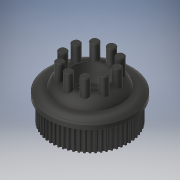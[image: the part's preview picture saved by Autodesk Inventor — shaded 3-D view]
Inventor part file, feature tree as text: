
AUTODESK INVENTOR PART (.ipt)
format: ipt  version: 2019.2 (Build 232265000, 265)  size: 961,536 bytes
history: native  units: mm
features: sketch x6, extrude x5, chamfer x4, fillet x3, other x1, pattern_circular x1, plane x1
ambient origin geometry x8: Origin, YZ Plane, XZ Plane, XY Plane, X Axis, Y Axis, Z Axis, Center Point
bodies: Solid1 (feature_tree)
feature tree (21):
  other  "gates_P60-3M-09AL.ipt"
  extrude  "Extrusion1"  Depth=7.0mm
  fillet  "Fillet1"  Radius=7.0mm
  extrude  "Extrusion2"  Depth=10.0mm
  chamfer  "Chamfer1"  Distance=18.0mm
  pattern_circular  "Circular Pattern1"  Count=10 Angle=360.0deg
  plane  "Work Plane1"
  sketch  "Sketch3"  dims[d9=0.5mm d10=2.0mm d11=45.0deg d12=100.0mm d13=360.0deg]
  extrude  "Extrusion3"  Depth=0.938mm
  chamfer  "Chamfer2"  Distance=2.4mm
  extrude  "Extrusion8"  Depth=7.0mm TaperAngle=0.0deg
  extrude  "Extrusion9"  Depth=7.0mm TaperAngle=45.0deg
  chamfer  "Chamfer5"  Distance=1.2mm
  fillet  "Fillet4"  Radius=10.0mm
  chamfer  "Chamfer6"  Distance=56.54mm
  fillet  "Fillet5"  Radius=11.0mm
  sketch  "Sketch1"  dims[d0=44.8mm d1=25.0mm d2=7.0mm d3=0.0mm]
  sketch  "Sketch2"  dims[d6=15.85mm d7=18.0mm d8=0.0mm]
  sketch  "Sketch4"  dims[d15=20.0mm d16=0.938mm]
  sketch  "Sketch2_1"  dims[d4=10.0mm d5=5.8mm]
  sketch  "Sketch11"  dims[d17=23.873241mm d18=2.4mm d19=7.0mm d20=0.0mm d24=2.4mm d25=1.0mm d26=45.0deg d50=1.2mm d52=10.0mm d53=56.54mm d54=11.0mm d55=0.0mm d56=10.0mm d57=0.0mm d60=3.0mm d61=2.0mm d62=45.0deg d63=7.0mm d71=9.5mm d72=14.65mm d73=45.0deg d74=7.0mm d75=5.0mm d76=0.0mm]
